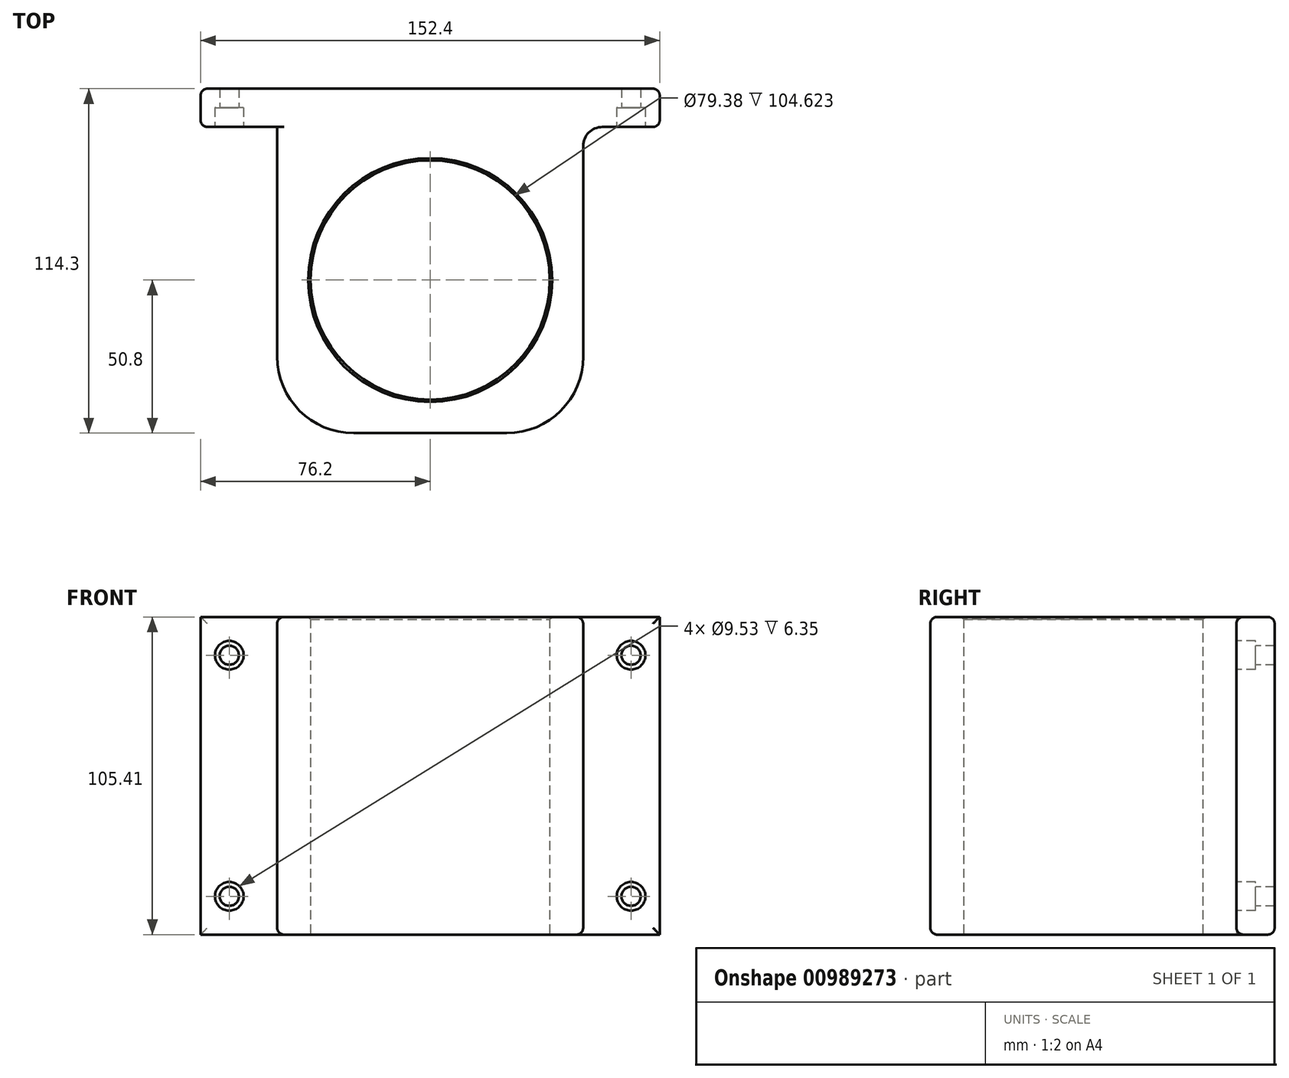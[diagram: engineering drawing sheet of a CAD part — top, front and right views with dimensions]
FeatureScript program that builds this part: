
annotation { "Feature Type Name" : "Feature", "Feature Type Description" : "" }
export const myFeature = defineFeature(function(context is Context, id is Id, definition is map)
    precondition{}
    {
        {
            var Q0;
            Q0=qCreatedBy(makeId("Front.planeOp"),FACE);
            var sketch = newSketch(context, id + "F0", { "sketchPlane" : qUnion([Q0])});
            skLineSegment(sketch, "E0.bottom", {"start": v(0, 0) * mm, "end": v(-152.4, 0) * mm});
            skLineSegment(sketch, "E0.top", {"start": v(0, 105.4) * mm, "end": v(-152.4, 105.4) * mm});
            skLineSegment(sketch, "E0.left", {"start": v(0, 0) * mm, "end": v(0, 105.4) * mm});
            skLineSegment(sketch, "E0.right", {"start": v(-152.4, 0) * mm, "end": v(-152.4, 105.4) * mm});
            skSolve(sketch);
        }
        {
            var Q0;
            Q0=makeQuery(id+"F0.imprint","IMPRINT",FACE,{"disambiguationData":[TD([[makeQuery(id+"F0.imprint","IMPRINT",EDGE,{"derivedFrom":sQuery(id+"F0.wireOp",EDGE,"E0.bottom")}),-1.0]])]});
            extrude(context, id + "F1", {"entities" : qUnion([Q0]), "depth" : 12.7 * mm, "offsetDistance" : 25.4 * mm});
        }
        {
            var Q0;
            Q0=makeQuery(id+"F1.opExtrude","CAP_FACE",FACE,{"disambiguationData":[OSD([sQuery(id+"F0.wireOp",EDGE,"E0.bottom"),sQuery(id+"F0.wireOp",EDGE,"E0.top"),sQuery(id+"F0.wireOp",EDGE,"E0.left"),sQuery(id+"F0.wireOp",EDGE,"E0.right")])],"isStart":false});
            var sketch = newSketch(context, id + "F2", { "sketchPlane" : qUnion([Q0])});
            skLineSegment(sketch, "E1", {"start": v(-76.2, 105.4) * mm, "end": v(-76.2, 0) * mm, "construction": true});
            skLineSegment(sketch, "E2", {"start": v(-152.4, 52.7) * mm, "end": v(0, 52.7) * mm, "construction": true});
            skPoint(sketch, "E3", {"position": v(-142.88, 12.7) * mm});
            skPoint(sketch, "E4", {"position": v(-142.88, 92.7) * mm});
            skPoint(sketch, "E5", {"position": v(-9.53, 92.71) * mm});
            skPoint(sketch, "E6", {"position": v(-9.53, 12.7) * mm});
            skSolve(sketch);
        }
        {
            var Q0;
            Q0=sQuery(id+"F2.wireOp",VERTEX,"E5");
            var Q1;
            Q1=sQuery(id+"F2.wireOp",VERTEX,"E4");
            var Q2;
            Q2=sQuery(id+"F2.wireOp",VERTEX,"E6");
            var Q3;
            Q3=sQuery(id+"F2.wireOp",VERTEX,"E3");
            var Q4;
            Q4=makeQuery(id+"F1.opExtrude","SWEPT_BODY",BODY,{"disambiguationData":[OSD([sQuery(id+"F0.wireOp",EDGE,"E0.bottom"),sQuery(id+"F0.wireOp",EDGE,"E0.top"),sQuery(id+"F0.wireOp",EDGE,"E0.left"),sQuery(id+"F0.wireOp",EDGE,"E0.right")])]});
            hole(context, id + "F3", {"style" : HoleStyle.C_BORE, "endStyle" : HoleEndStyle.THROUGH, "holeDiameter" : 6.35 * mm, "cBoreDiameter" : 9.52 * mm, "cBoreDepth" : 6.35 * mm, "majorDiameter" : 6.35 * mm, "isTappedThrough" : true, "tappedDepth" : 12.7 * mm, "tapClearance" : 3, "startFromSketch" : true, "locations" : qUnion([Q0, Q1, Q2, Q3]), "scope" : qUnion([Q4])});
        }
        {
            var Q0;
            Q0=makeQuery(id+"F1.opExtrude","CAP_FACE",FACE,{"disambiguationData":[OSD([sQuery(id+"F0.wireOp",EDGE,"E0.bottom"),sQuery(id+"F0.wireOp",EDGE,"E0.top"),sQuery(id+"F0.wireOp",EDGE,"E0.left"),sQuery(id+"F0.wireOp",EDGE,"E0.right")])],"isStart":false});
            var sketch = newSketch(context, id + "F4", { "sketchPlane" : qUnion([Q0])});
            skLineSegment(sketch, "E7", {"start": v(-127, 105.4) * mm, "end": v(-127, 0) * mm});
            skLineSegment(sketch, "E8", {"start": v(-25.4, 105.4) * mm, "end": v(-25.4, 0) * mm});
            skSolve(sketch);
        }
        {
            var Q0;
            {var subQ0=sQuery(id+"F4.wireOp",EDGE,"E7");Q0=makeQuery(id+"F4.imprint","IMPRINT",FACE,{"disambiguationData":[TD([[makeQuery(id+"F4.imprint","IMPRINT",EDGE,{"derivedFrom":subQ0}),1.0]])]});}
            extrude(context, id + "F5", {"entities" : qUnion([Q0]), "operationType" : NewBodyOperationType.ADD, "depth" : 101.6 * mm, "offsetDistance" : 25.4 * mm});
        }
        {
            var Q0;
            Q0=makeQuery(id+"F5.opExtrude","CAP_EDGE",EDGE,{"disambiguationData":[OSD([sQuery(id+"F4.wireOp",EDGE,"E8")])],"isStart":false});
            var Q1;
            Q1=makeQuery(id+"F5.opExtrude","CAP_EDGE",EDGE,{"disambiguationData":[OSD([sQuery(id+"F4.wireOp",EDGE,"E7")])],"isStart":false});
            fillet(context, id + "F6", {"entities" : qUnion([Q0, Q1]), "tangentPropagation" : true, "radius" : 25.4 * mm, "defaultsChanged" : true, "vertexSettings" : [], "allowEdgeOverflow" : false});
        }
        {
            var Q0;
            Q0=makeQuery(id+"F5.opExtrude","CAP_EDGE",EDGE,{"disambiguationData":[OSD([sQuery(id+"F4.wireOp",EDGE,"E8")])],"isStart":true});
            var Q1;
            Q1=makeQuery(id+"F5.opExtrude","CAP_EDGE",EDGE,{"disambiguationData":[OSD([sQuery(id+"F4.wireOp",EDGE,"E7")])],"isStart":true});
            fillet(context, id + "F7", {"entities" : qUnion([Q0, Q1]), "tangentPropagation" : true, "radius" : 6.35 * mm, "defaultsChanged" : true, "vertexSettings" : [], "allowEdgeOverflow" : false});
        }
        {
            var Q0;
            {var subQ0=sQuery(id+"F0.wireOp",EDGE,"E0.bottom");Q0=makeQuery(id+"F5.boolean.opBoolean","MERGE",FACE,{"derivedFrom":[makeQuery(id+"F1.opExtrude","SWEPT_FACE",FACE,{"disambiguationData":[OSD([subQ0])]}),makeQuery(id+"F5.opExtrude","SWEPT_FACE",FACE,{"disambiguationData":[OSD([subQ0])]})]});}
            var sketch = newSketch(context, id + "F8", { "sketchPlane" : qUnion([Q0])});
            skCircle(sketch, "E9", {"center": v(-76.2, 63.5) * mm, "radius": 39.69 * mm});
            skSolve(sketch);
        }
        {
            var Q0;
            Q0 = qSketchRegion(id + "F8", true);
            extrude(context, id + "F9", {"entities" : qUnion([Q0]), "operationType" : NewBodyOperationType.REMOVE, "endBound" : BoundingType.THROUGH_ALL, "oppositeDirection" : true, "depth" : 25.4 * mm, "offsetDistance" : 25.4 * mm});
        }
        {
            var Q0;
            {var subQ0=sQuery(id+"F0.wireOp",EDGE,"E0.left");var subQ1=sQuery(id+"F0.wireOp",EDGE,"E0.bottom");Q0=makeQuery(id+"F5.boolean.opBoolean","SPLIT",EDGE,{"disambiguationData":[TD([makeQuery(id+"F1.opExtrude","SWEPT_FACE",FACE,{"disambiguationData":[OSD([subQ0])]})])],"derivedFrom":makeQuery(id+"F1.opExtrude","CAP_EDGE",EDGE,{"disambiguationData":[OSD([subQ1])],"isStart":false})});}
            var Q1;
            Q1=makeQuery(id+"F1.opExtrude","CAP_EDGE",EDGE,{"disambiguationData":[OSD([sQuery(id+"F0.wireOp",EDGE,"E0.left")])],"isStart":false});
            var Q2;
            {var subQ0=sQuery(id+"F0.wireOp",EDGE,"E0.left");var subQ1=sQuery(id+"F0.wireOp",EDGE,"E0.top");Q2=makeQuery(id+"F5.boolean.opBoolean","SPLIT",EDGE,{"disambiguationData":[TD([makeQuery(id+"F1.opExtrude","SWEPT_FACE",FACE,{"disambiguationData":[OSD([subQ0])]})])],"derivedFrom":makeQuery(id+"F1.opExtrude","CAP_EDGE",EDGE,{"disambiguationData":[OSD([subQ1])],"isStart":false})});}
            var Q3;
            Q3=makeQuery(id+"F1.opExtrude","CAP_EDGE",EDGE,{"disambiguationData":[OSD([sQuery(id+"F0.wireOp",EDGE,"E0.top")])],"isStart":true});
            var Q4;
            Q4=makeQuery(id+"F1.opExtrude","CAP_EDGE",EDGE,{"disambiguationData":[OSD([sQuery(id+"F0.wireOp",EDGE,"E0.left")])],"isStart":true});
            var Q5;
            Q5=makeQuery(id+"F1.opExtrude","CAP_EDGE",EDGE,{"disambiguationData":[OSD([sQuery(id+"F0.wireOp",EDGE,"E0.right")])],"isStart":false});
            var Q6;
            Q6=makeQuery(id+"F1.opExtrude","CAP_EDGE",EDGE,{"disambiguationData":[OSD([sQuery(id+"F0.wireOp",EDGE,"E0.right")])],"isStart":true});
            var Q7;
            Q7=makeQuery(id+"F1.opExtrude","CAP_EDGE",EDGE,{"disambiguationData":[OSD([sQuery(id+"F0.wireOp",EDGE,"E0.bottom")])],"isStart":true});
            fillet(context, id + "F10", {"entities" : qUnion([Q0, Q1, Q2, Q3, Q4, Q5, Q6, Q7]), "tangentPropagation" : true, "radius" : 2.3 * mm, "defaultsChanged" : false, "vertexSettings" : [], "allowEdgeOverflow" : false});
        }
        {
            var Q0;
            {var subQ0=sQuery(id+"F0.wireOp",EDGE,"E0.top");Q0=makeQuery(id+"F9.boolean.opBoolean","INTERSECT",EDGE,{"derivedFrom":[makeQuery(id+"F5.boolean.opBoolean","MERGE",FACE,{"derivedFrom":[makeQuery(id+"F1.opExtrude","SWEPT_FACE",FACE,{"disambiguationData":[OSD([subQ0])]}),makeQuery(id+"F5.opExtrude","SWEPT_FACE",FACE,{"disambiguationData":[OSD([subQ0])]})]}),makeQuery(id+"F9.opExtrude","SWEPT_FACE",FACE,{"disambiguationData":[OSD([sQuery(id+"F8.wireOp",EDGE,"E9")])]})]});}
            var Q1;
            Q1=makeQuery(id+"F9.boolean.opBoolean","COPY",EDGE,{"derivedFrom":makeQuery(id+"F9.opExtrude","CAP_EDGE",EDGE,{"disambiguationData":[OSD([sQuery(id+"F8.wireOp",EDGE,"E9")])],"isStart":true})});
            chamfer(context, id + "F11", {"entities" : qUnion([Q0, Q1]), "width" : 0.79 * mm, "tangentPropagation" : true});
        }
    });
